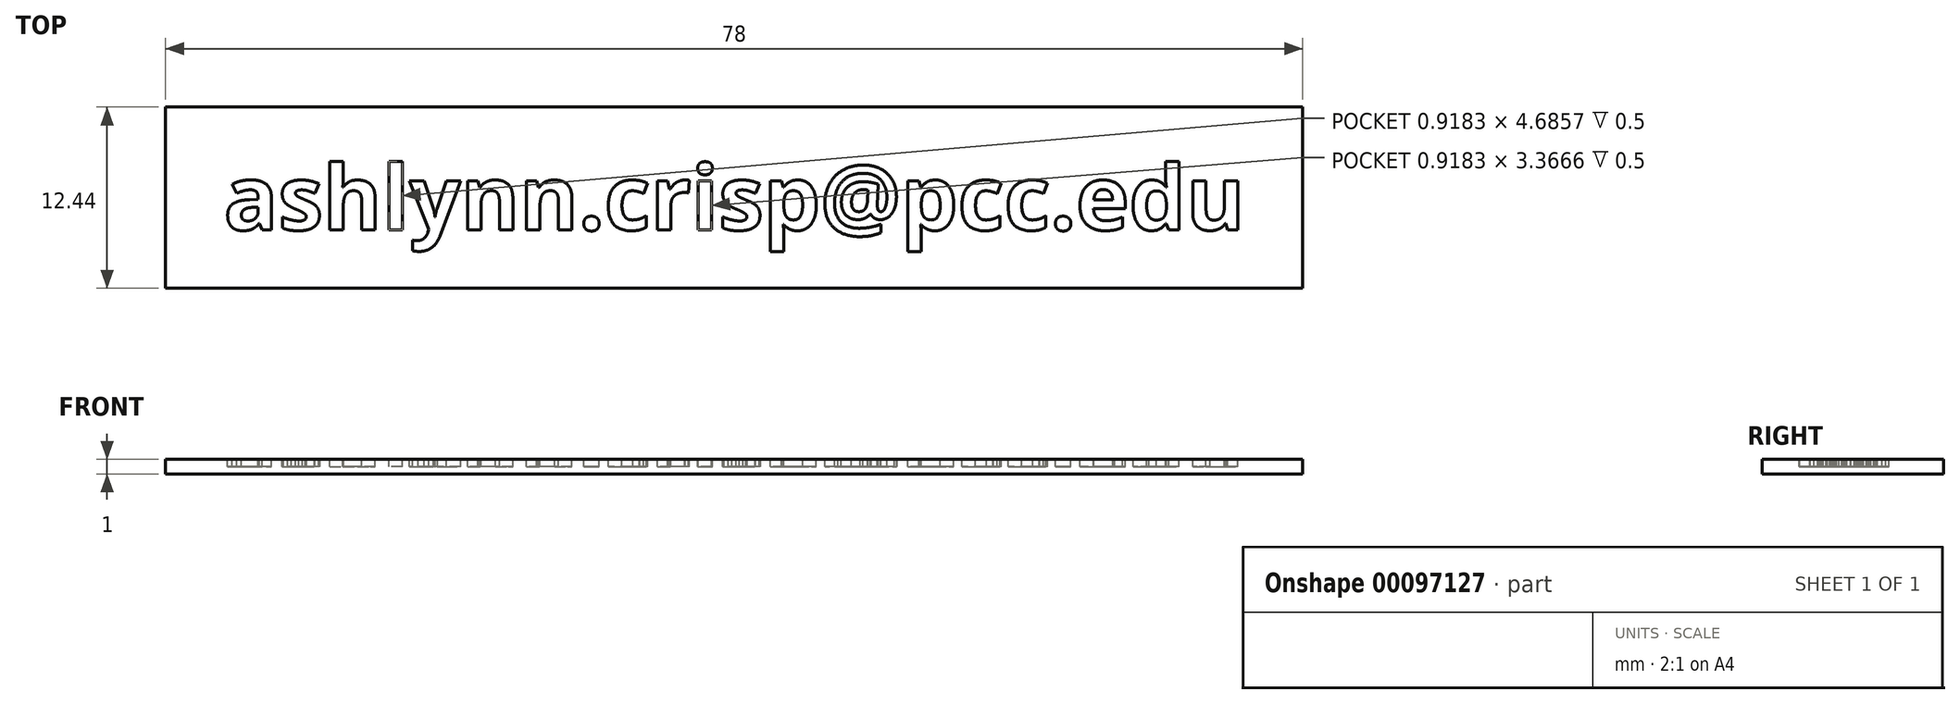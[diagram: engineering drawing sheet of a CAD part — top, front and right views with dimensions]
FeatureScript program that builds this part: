
annotation { "Feature Type Name" : "Feature", "Feature Type Description" : "" }
export const myFeature = defineFeature(function(context is Context, id is Id, definition is map)
    precondition{}
    {
        {
            var Q0;
            Q0=qCreatedBy(makeId("Top.planeOp"),FACE);
            var sketch = newSketch(context, id + "F0", { "sketchPlane" : qUnion([Q0])});
            skText(sketch, "E0", { "text": "<email>", "fontName": "OpenSans-Bold.ttf"});
            skLineSegment(sketch, "E1.bottom", {"start": v(-39, 8.44) * mm, "end": v(39, 8.44) * mm});
            skLineSegment(sketch, "E1.top", {"start": v(-39, -4) * mm, "end": v(39, -4) * mm});
            skLineSegment(sketch, "E1.left", {"start": v(-39, 8.44) * mm, "end": v(-39, -4) * mm});
            skLineSegment(sketch, "E1.right", {"start": v(39, 8.44) * mm, "end": v(39, -4) * mm});
            skPoint(sketch, "E2", {"position": v(0, 8.44) * mm});
            skPoint(sketch, "E3", {"position": v(39, 2.22) * mm});
            skPoint(sketch, "E4", {"position": v(35, 2.22) * mm});
            const initialGuessF0  = {"E0": [-0.035, 0, 1, 0, 0.00444]};
            skSetInitialGuess(sketch, initialGuessF0);
            skSolve(sketch);
        }
        {
            var Q0;
            Q0 = qSketchRegion(id + "F0", true);
            var Q1;
            Q1=makeQuery(id+"F0.imprint","IMPRINT",FACE,{"disambiguationData":[TD([[makeQuery(id+"F0.imprint","IMPRINT",EDGE,{"derivedFrom":sQuery(id+"F0.wireOp",EDGE,"E0.sketch_text.stroke-283")}),-1.0]])]});
            var Q2;
            Q2=makeQuery(id+"F0.imprint","IMPRINT",FACE,{"disambiguationData":[TD([[makeQuery(id+"F0.imprint","IMPRINT",EDGE,{"derivedFrom":sQuery(id+"F0.wireOp",EDGE,"E0.sketch_text.stroke-353")}),1.0]])]});
            var Q3;
            Q3=makeQuery(id+"F0.imprint","IMPRINT",FACE,{"disambiguationData":[TD([[makeQuery(id+"F0.imprint","IMPRINT",EDGE,{"derivedFrom":sQuery(id+"F0.wireOp",EDGE,"E0.sketch_text.stroke-362")}),-1.0]])]});
            var Q4;
            Q4=makeQuery(id+"F0.imprint","IMPRINT",FACE,{"disambiguationData":[TD([[makeQuery(id+"F0.imprint","IMPRINT",EDGE,{"derivedFrom":sQuery(id+"F0.wireOp",EDGE,"E0.sketch_text.stroke-0")}),-1.0]])]});
            var Q5;
            Q5=makeQuery(id+"F0.imprint","IMPRINT",FACE,{"disambiguationData":[TD([[makeQuery(id+"F0.imprint","IMPRINT",EDGE,{"derivedFrom":sQuery(id+"F0.wireOp",EDGE,"E0.sketch_text.stroke-275")}),1.0]])]});
            var Q6;
            Q6=makeQuery(id+"F0.imprint","IMPRINT",FACE,{"disambiguationData":[TD([[makeQuery(id+"F0.imprint","IMPRINT",EDGE,{"derivedFrom":sQuery(id+"F0.wireOp",EDGE,"E0.sketch_text.stroke-72")}),-1.0]])]});
            var Q7;
            Q7=makeQuery(id+"F0.imprint","IMPRINT",FACE,{"disambiguationData":[TD([[makeQuery(id+"F0.imprint","IMPRINT",EDGE,{"derivedFrom":sQuery(id+"F0.wireOp",EDGE,"E0.sketch_text.stroke-89")}),-1.0]])]});
            var Q8;
            Q8=makeQuery(id+"F0.imprint","IMPRINT",FACE,{"disambiguationData":[TD([[makeQuery(id+"F0.imprint","IMPRINT",EDGE,{"derivedFrom":sQuery(id+"F0.wireOp",EDGE,"E0.sketch_text.stroke-106")}),-1.0]])]});
            var Q9;
            Q9=makeQuery(id+"F0.imprint","IMPRINT",FACE,{"disambiguationData":[TD([[makeQuery(id+"F0.imprint","IMPRINT",EDGE,{"derivedFrom":sQuery(id+"F0.wireOp",EDGE,"E0.sketch_text.stroke-131")}),-1.0]])]});
            var Q10;
            Q10=makeQuery(id+"F0.imprint","IMPRINT",FACE,{"disambiguationData":[TD([[makeQuery(id+"F0.imprint","IMPRINT",EDGE,{"derivedFrom":sQuery(id+"F0.wireOp",EDGE,"E0.sketch_text.stroke-193")}),-1.0]])]});
            var Q11;
            Q11=makeQuery(id+"F0.imprint","IMPRINT",FACE,{"disambiguationData":[TD([[makeQuery(id+"F0.imprint","IMPRINT",EDGE,{"derivedFrom":sQuery(id+"F0.wireOp",EDGE,"E0.sketch_text.stroke-0")}),1.0]])]});
            var Q12;
            Q12=makeQuery(id+"F0.imprint","IMPRINT",FACE,{"disambiguationData":[TD([[makeQuery(id+"F0.imprint","IMPRINT",EDGE,{"derivedFrom":sQuery(id+"F0.wireOp",EDGE,"E0.sketch_text.stroke-339")}),-1.0]])]});
            var Q13;
            Q13=makeQuery(id+"F0.imprint","IMPRINT",FACE,{"disambiguationData":[TD([[makeQuery(id+"F0.imprint","IMPRINT",EDGE,{"derivedFrom":sQuery(id+"F0.wireOp",EDGE,"E0.sketch_text.stroke-319")}),-1.0]])]});
            var Q14;
            Q14=makeQuery(id+"F0.imprint","IMPRINT",FACE,{"disambiguationData":[TD([[makeQuery(id+"F0.imprint","IMPRINT",EDGE,{"derivedFrom":sQuery(id+"F0.wireOp",EDGE,"E0.sketch_text.stroke-260")}),-1.0]])]});
            var Q15;
            Q15=makeQuery(id+"F0.imprint","IMPRINT",FACE,{"disambiguationData":[TD([[makeQuery(id+"F0.imprint","IMPRINT",EDGE,{"derivedFrom":sQuery(id+"F0.wireOp",EDGE,"E0.sketch_text.stroke-297")}),-1.0]])]});
            var Q16;
            Q16=makeQuery(id+"F0.imprint","IMPRINT",FACE,{"disambiguationData":[TD([[makeQuery(id+"F0.imprint","IMPRINT",EDGE,{"derivedFrom":sQuery(id+"F0.wireOp",EDGE,"E0.sketch_text.stroke-311")}),-1.0]])]});
            var Q17;
            Q17=makeQuery(id+"F0.imprint","IMPRINT",FACE,{"disambiguationData":[TD([[makeQuery(id+"F0.imprint","IMPRINT",EDGE,{"derivedFrom":sQuery(id+"F0.wireOp",EDGE,"E0.sketch_text.stroke-319")}),1.0]])]});
            var Q18;
            Q18=makeQuery(id+"F0.imprint","IMPRINT",FACE,{"disambiguationData":[TD([[makeQuery(id+"F0.imprint","IMPRINT",EDGE,{"derivedFrom":sQuery(id+"F0.wireOp",EDGE,"E0.sketch_text.stroke-208")}),1.0]])]});
            var Q19;
            Q19=makeQuery(id+"F0.imprint","IMPRINT",FACE,{"disambiguationData":[TD([[makeQuery(id+"F0.imprint","IMPRINT",EDGE,{"derivedFrom":sQuery(id+"F0.wireOp",EDGE,"E0.sketch_text.stroke-253")}),1.0]])]});
            var Q20;
            Q20=makeQuery(id+"F0.imprint","IMPRINT",FACE,{"disambiguationData":[TD([[makeQuery(id+"F0.imprint","IMPRINT",EDGE,{"derivedFrom":sQuery(id+"F0.wireOp",EDGE,"E0.sketch_text.stroke-18")}),1.0]])]});
            var Q21;
            Q21=makeQuery(id+"F0.imprint","IMPRINT",FACE,{"disambiguationData":[TD([[makeQuery(id+"F0.imprint","IMPRINT",EDGE,{"derivedFrom":sQuery(id+"F0.wireOp",EDGE,"E0.sketch_text.stroke-25")}),-1.0]])]});
            var Q22;
            Q22=makeQuery(id+"F0.imprint","IMPRINT",FACE,{"disambiguationData":[TD([[makeQuery(id+"F0.imprint","IMPRINT",EDGE,{"derivedFrom":sQuery(id+"F0.wireOp",EDGE,"E0.sketch_text.stroke-51")}),-1.0]])]});
            var Q23;
            Q23=makeQuery(id+"F0.imprint","IMPRINT",FACE,{"disambiguationData":[TD([[makeQuery(id+"F0.imprint","IMPRINT",EDGE,{"derivedFrom":sQuery(id+"F0.wireOp",EDGE,"E0.sketch_text.stroke-68")}),-1.0]])]});
            var Q24;
            Q24=makeQuery(id+"F0.imprint","IMPRINT",FACE,{"disambiguationData":[TD([[makeQuery(id+"F0.imprint","IMPRINT",EDGE,{"derivedFrom":sQuery(id+"F0.wireOp",EDGE,"E0.sketch_text.stroke-123")}),-1.0]])]});
            var Q25;
            Q25=makeQuery(id+"F0.imprint","IMPRINT",FACE,{"disambiguationData":[TD([[makeQuery(id+"F0.imprint","IMPRINT",EDGE,{"derivedFrom":sQuery(id+"F0.wireOp",EDGE,"E0.sketch_text.stroke-145")}),-1.0]])]});
            var Q26;
            Q26=makeQuery(id+"F0.imprint","IMPRINT",FACE,{"disambiguationData":[TD([[makeQuery(id+"F0.imprint","IMPRINT",EDGE,{"derivedFrom":sQuery(id+"F0.wireOp",EDGE,"E0.sketch_text.stroke-158")}),-1.0]])]});
            var Q27;
            Q27=makeQuery(id+"F0.imprint","IMPRINT",FACE,{"disambiguationData":[TD([[makeQuery(id+"F0.imprint","IMPRINT",EDGE,{"derivedFrom":sQuery(id+"F0.wireOp",EDGE,"E0.sketch_text.stroke-163")}),-1.0]])]});
            var Q28;
            Q28=makeQuery(id+"F0.imprint","IMPRINT",FACE,{"disambiguationData":[TD([[makeQuery(id+"F0.imprint","IMPRINT",EDGE,{"derivedFrom":sQuery(id+"F0.wireOp",EDGE,"E0.sketch_text.stroke-167")}),-1.0]])]});
            var Q29;
            Q29=makeQuery(id+"F0.imprint","IMPRINT",FACE,{"disambiguationData":[TD([[makeQuery(id+"F0.imprint","IMPRINT",EDGE,{"derivedFrom":sQuery(id+"F0.wireOp",EDGE,"E0.sketch_text.stroke-216")}),-1.0]])]});
            extrude(context, id + "F1", {"entities" : qUnion([Q0, Q1, Q2, Q3, Q4, Q5, Q6, Q7, Q8, Q9, Q10, Q11, Q12, Q13, Q14, Q15, Q16, Q17, Q18, Q19, Q20, Q21, Q22, Q23, Q24, Q25, Q26, Q27, Q28, Q29]), "oppositeDirection" : true, "depth" : 1 * mm});
        }
        {
            var Q0;
            Q0=makeQuery(id+"F0.imprint","IMPRINT",FACE,{"disambiguationData":[TD([[makeQuery(id+"F0.imprint","IMPRINT",EDGE,{"derivedFrom":sQuery(id+"F0.wireOp",EDGE,"E0.sketch_text.stroke-0")}),-1.0]])]});
            var Q1;
            Q1=makeQuery(id+"F0.imprint","IMPRINT",FACE,{"disambiguationData":[TD([[makeQuery(id+"F0.imprint","IMPRINT",EDGE,{"derivedFrom":sQuery(id+"F0.wireOp",EDGE,"E0.sketch_text.stroke-25")}),-1.0]])]});
            var Q2;
            Q2=makeQuery(id+"F0.imprint","IMPRINT",FACE,{"disambiguationData":[TD([[makeQuery(id+"F0.imprint","IMPRINT",EDGE,{"derivedFrom":sQuery(id+"F0.wireOp",EDGE,"E0.sketch_text.stroke-51")}),-1.0]])]});
            var Q3;
            Q3=makeQuery(id+"F0.imprint","IMPRINT",FACE,{"disambiguationData":[TD([[makeQuery(id+"F0.imprint","IMPRINT",EDGE,{"derivedFrom":sQuery(id+"F0.wireOp",EDGE,"E0.sketch_text.stroke-68")}),-1.0]])]});
            var Q4;
            Q4=makeQuery(id+"F0.imprint","IMPRINT",FACE,{"disambiguationData":[TD([[makeQuery(id+"F0.imprint","IMPRINT",EDGE,{"derivedFrom":sQuery(id+"F0.wireOp",EDGE,"E0.sketch_text.stroke-72")}),-1.0]])]});
            var Q5;
            Q5=makeQuery(id+"F0.imprint","IMPRINT",FACE,{"disambiguationData":[TD([[makeQuery(id+"F0.imprint","IMPRINT",EDGE,{"derivedFrom":sQuery(id+"F0.wireOp",EDGE,"E0.sketch_text.stroke-89")}),-1.0]])]});
            var Q6;
            Q6=makeQuery(id+"F0.imprint","IMPRINT",FACE,{"disambiguationData":[TD([[makeQuery(id+"F0.imprint","IMPRINT",EDGE,{"derivedFrom":sQuery(id+"F0.wireOp",EDGE,"E0.sketch_text.stroke-106")}),-1.0]])]});
            var Q7;
            Q7=makeQuery(id+"F0.imprint","IMPRINT",FACE,{"disambiguationData":[TD([[makeQuery(id+"F0.imprint","IMPRINT",EDGE,{"derivedFrom":sQuery(id+"F0.wireOp",EDGE,"E0.sketch_text.stroke-123")}),-1.0]])]});
            var Q8;
            Q8=makeQuery(id+"F0.imprint","IMPRINT",FACE,{"disambiguationData":[TD([[makeQuery(id+"F0.imprint","IMPRINT",EDGE,{"derivedFrom":sQuery(id+"F0.wireOp",EDGE,"E0.sketch_text.stroke-131")}),-1.0]])]});
            var Q9;
            Q9=makeQuery(id+"F0.imprint","IMPRINT",FACE,{"disambiguationData":[TD([[makeQuery(id+"F0.imprint","IMPRINT",EDGE,{"derivedFrom":sQuery(id+"F0.wireOp",EDGE,"E0.sketch_text.stroke-145")}),-1.0]])]});
            var Q10;
            Q10=makeQuery(id+"F0.imprint","IMPRINT",FACE,{"disambiguationData":[TD([[makeQuery(id+"F0.imprint","IMPRINT",EDGE,{"derivedFrom":sQuery(id+"F0.wireOp",EDGE,"E0.sketch_text.stroke-158")}),-1.0]])]});
            var Q11;
            Q11=makeQuery(id+"F0.imprint","IMPRINT",FACE,{"disambiguationData":[TD([[makeQuery(id+"F0.imprint","IMPRINT",EDGE,{"derivedFrom":sQuery(id+"F0.wireOp",EDGE,"E0.sketch_text.stroke-163")}),-1.0]])]});
            var Q12;
            Q12=makeQuery(id+"F0.imprint","IMPRINT",FACE,{"disambiguationData":[TD([[makeQuery(id+"F0.imprint","IMPRINT",EDGE,{"derivedFrom":sQuery(id+"F0.wireOp",EDGE,"E0.sketch_text.stroke-167")}),-1.0]])]});
            var Q13;
            Q13=makeQuery(id+"F0.imprint","IMPRINT",FACE,{"disambiguationData":[TD([[makeQuery(id+"F0.imprint","IMPRINT",EDGE,{"derivedFrom":sQuery(id+"F0.wireOp",EDGE,"E0.sketch_text.stroke-193")}),-1.0]])]});
            var Q14;
            Q14=makeQuery(id+"F0.imprint","IMPRINT",FACE,{"disambiguationData":[TD([[makeQuery(id+"F0.imprint","IMPRINT",EDGE,{"derivedFrom":sQuery(id+"F0.wireOp",EDGE,"E0.sketch_text.stroke-216")}),-1.0]])]});
            var Q15;
            Q15=makeQuery(id+"F0.imprint","IMPRINT",FACE,{"disambiguationData":[TD([[makeQuery(id+"F0.imprint","IMPRINT",EDGE,{"derivedFrom":sQuery(id+"F0.wireOp",EDGE,"E0.sketch_text.stroke-260")}),-1.0]])]});
            var Q16;
            Q16=makeQuery(id+"F0.imprint","IMPRINT",FACE,{"disambiguationData":[TD([[makeQuery(id+"F0.imprint","IMPRINT",EDGE,{"derivedFrom":sQuery(id+"F0.wireOp",EDGE,"E0.sketch_text.stroke-311")}),-1.0]])]});
            var Q17;
            Q17=makeQuery(id+"F0.imprint","IMPRINT",FACE,{"disambiguationData":[TD([[makeQuery(id+"F0.imprint","IMPRINT",EDGE,{"derivedFrom":sQuery(id+"F0.wireOp",EDGE,"E0.sketch_text.stroke-319")}),-1.0]])]});
            var Q18;
            Q18=makeQuery(id+"F0.imprint","IMPRINT",FACE,{"disambiguationData":[TD([[makeQuery(id+"F0.imprint","IMPRINT",EDGE,{"derivedFrom":sQuery(id+"F0.wireOp",EDGE,"E0.sketch_text.stroke-339")}),-1.0]])]});
            var Q19;
            Q19=makeQuery(id+"F0.imprint","IMPRINT",FACE,{"disambiguationData":[TD([[makeQuery(id+"F0.imprint","IMPRINT",EDGE,{"derivedFrom":sQuery(id+"F0.wireOp",EDGE,"E0.sketch_text.stroke-362")}),-1.0]])]});
            var Q20;
            Q20=makeQuery(id+"F0.imprint","IMPRINT",FACE,{"disambiguationData":[TD([[makeQuery(id+"F0.imprint","IMPRINT",EDGE,{"derivedFrom":sQuery(id+"F0.wireOp",EDGE,"E0.sketch_text.stroke-283")}),-1.0]])]});
            var Q21;
            Q21=makeQuery(id+"F0.imprint","IMPRINT",FACE,{"disambiguationData":[TD([[makeQuery(id+"F0.imprint","IMPRINT",EDGE,{"derivedFrom":sQuery(id+"F0.wireOp",EDGE,"E0.sketch_text.stroke-297")}),-1.0]])]});
            extrude(context, id + "F2", {"entities" : qUnion([Q0, Q1, Q2, Q3, Q4, Q5, Q6, Q7, Q8, Q9, Q10, Q11, Q12, Q13, Q14, Q15, Q16, Q17, Q18, Q19, Q20, Q21]), "operationType" : NewBodyOperationType.REMOVE, "oppositeDirection" : true, "depth" : 0.5 * mm});
        }
    });
